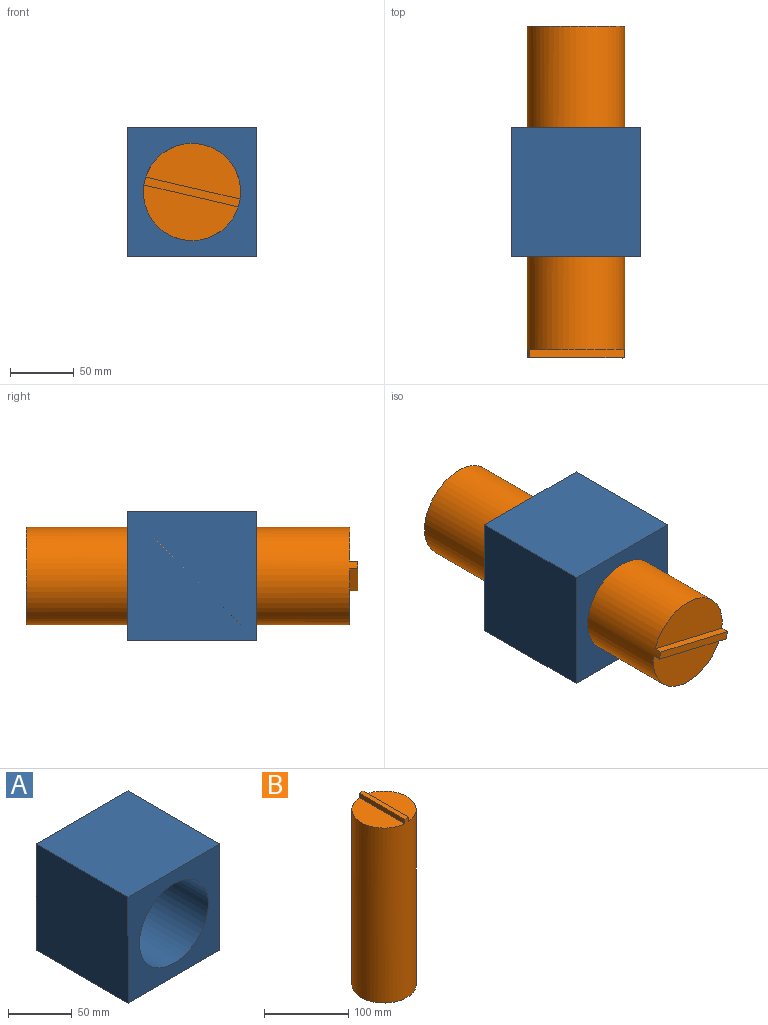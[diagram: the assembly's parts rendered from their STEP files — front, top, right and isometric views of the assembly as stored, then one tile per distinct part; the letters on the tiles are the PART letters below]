
ASSEMBLY  parts=2 mates=1
PART A: 7 faces, bbox 101.6x101.6x101.6 mm
  f0: plane 101.6x101.6mm, normal (-1,0,0), area 10322.6mm2, adj f1,f3,f5,f6
  f1: plane 101.6x101.6mm, normal (0,0,-1), area 10322.6mm2, adj f0,f2,f5,f6
  f2: plane 101.6x101.6mm, normal (1,0,0), area 10322.6mm2, adj f1,f3,f5,f6
  f3: plane 101.6x101.6mm, normal (0,0,1), area 10322.6mm2, adj f0,f2,f5,f6
  f4: cylinder r=38.1mm len=101.6mm, axis (0,1,0), area 24322mm2, adj f5,f6
  f5: plane 101.6x101.6mm, normal (0,-1,0), area 5762.2mm2, adj f0,f1,f2,f3,f4
  f6: plane 101.6x101.6mm, normal (0,1,0), area 5762.2mm2, adj f0,f1,f2,f3,f4
PART B: 7 faces, bbox 76.2x76.2x260.4 mm
  f0: plane 75.94x34.93mm, normal (0,0,1), area 2038.5mm2, adj f1,f5
  f1: cylinder r=38.1mm len=260.35mm, axis (0,0,-1), area 60885.6mm2, adj f0,f2,f3,f4,f5,f6
  f2: plane 75.94x34.93mm, normal (0,0,1), area 2038.5mm2, adj f1,f4
  f3: plane 76.2x76.2mm, normal (0,0,-1), area 4560.4mm2, adj f1
  f4: plane 75.94x6.35mm, normal (-1,0,0), area 482.2mm2, adj f1,f2,f6
  f5: plane 75.94x6.35mm, normal (1,0,0), area 482.2mm2, adj f0,f1,f6
  f6: plane 76.2x6.35mm, normal (0,0,1), area 483.3mm2, adj f1,f4,f5
PLACE A t=(-50.8,50.8,0)mm
PLACE B rot(axis=(0.67,-0.53,0.53),112.7deg) t=(0,130.18,50.8)mm
MATE revolute A.f4 <-> B.f1  axis (0,1,0) through (0,0,50.8)mm
